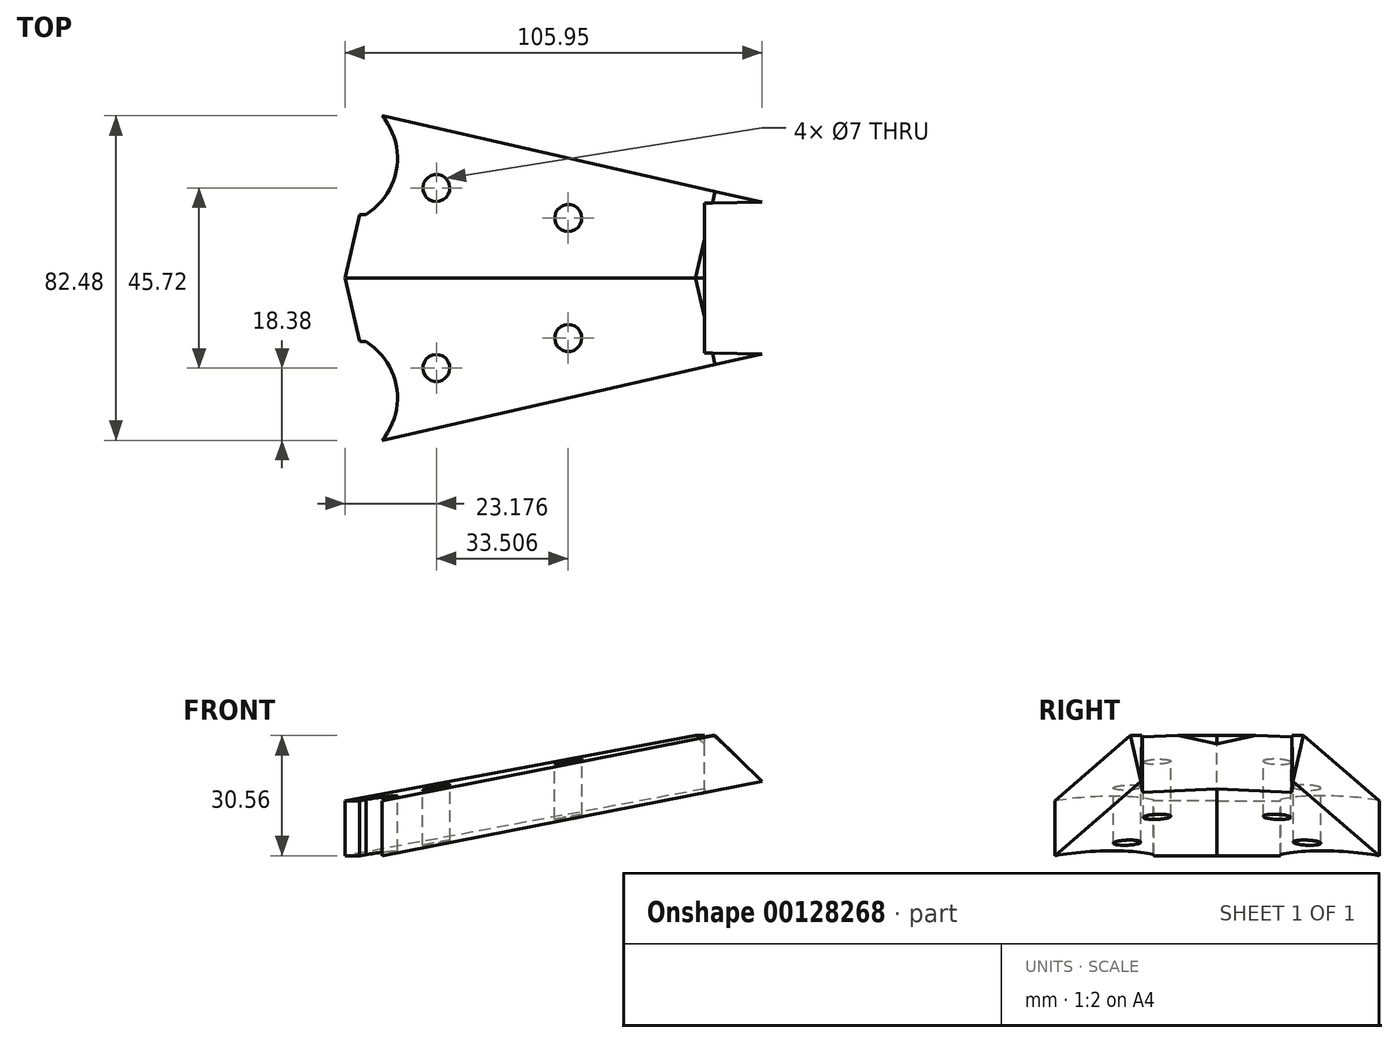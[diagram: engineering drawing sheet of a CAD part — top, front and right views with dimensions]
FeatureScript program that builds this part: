
annotation { "Feature Type Name" : "Feature", "Feature Type Description" : "" }
export const myFeature = defineFeature(function(context is Context, id is Id, definition is map)
    precondition{}
    {
        {
            var Q0;
            Q0=qCreatedBy(makeId("Top.planeOp"),FACE);
            var sketch = newSketch(context, id + "F0", { "sketchPlane" : qUnion([Q0])});
            skLineSegment(sketch, "E0", {"start": v(-293, 0) * mm, "end": v(-293, -19) * mm});
            skPoint(sketch, "E1.end.orphan", {"position": v(0, -123.72) * mm});
            skLineSegment(sketch, "E2", {"start": v(-293, -19) * mm, "end": v(-278.32, -19.28) * mm});
            skLineSegment(sketch, "E3", {"start": v(-394.6, -45.72) * mm, "end": v(-394.6, 0) * mm});
            skLineSegment(sketch, "E4", {"start": v(-293, 0) * mm, "end": v(-394.6, 0) * mm});
            skLineSegment(sketch, "E5", {"start": v(-394.6, -45.72) * mm, "end": v(-278.32, -19.28) * mm});
            skPoint(sketch, "E6.end.orphan", {"position": v(0, 0) * mm});
            skPoint(sketch, "E6.start.orphan", {"position": v(0, -24.5) * mm});
            skCircle(sketch, "E7", {"center": v(-361.1, -22.86) * mm, "radius": 3.5 * mm});
            skCircle(sketch, "E8", {"center": v(-327.59, -15.24) * mm, "radius": 3.5 * mm});
            skArc(sketch, "E9", {"start": v(-394.6, 0) * mm, "mid": v(-390.09, -11.3) * mm, "end": v(-378.93, -16.18) * mm});
            skPoint(sketch, "E9.second.point", {"position": v(-362.57, 0) * mm});
            skPoint(sketch, "E9.third.point", {"position": v(-378.93, -16.18) * mm});
            skArc(sketch, "E10", {"start": v(-374.89, -41.24) * mm, "mid": v(-371.17, -27.78) * mm, "end": v(-378.93, -16.18) * mm});
            skPoint(sketch, "E10.second.point", {"position": v(-374.89, -41.24) * mm});
            skSolve(sketch);
        }
        {
            var Q0;
            {var subQ0=sQuery(id+"F0.wireOp",EDGE,"E0");Q0=makeQuery(id+"F0.imprint","IMPRINT",FACE,{"disambiguationData":[TD([[makeQuery(id+"F0.imprint","IMPRINT",EDGE,{"derivedFrom":subQ0}),-1.0]])]});}
            extrude(context, id + "F1", {"entities" : qUnion([Q0]), "oppositeDirection" : true, "depth" : 32.9 * mm});
        }
        {
            var Q0;
            Q0=makeQuery(id+"F1.opExtrude","SWEPT_FACE",FACE,{"disambiguationData":[OSD([sQuery(id+"F0.wireOp",EDGE,"E5")])]});
            var sketch = newSketch(context, id + "F2", { "sketchPlane" : qUnion([Q0])});
            skPoint(sketch, "E11.end.orphan", {"position": v(-325.18, 0) * mm});
            skLineSegment(sketch, "E12", {"start": v(-287.9, -2.33) * mm, "end": v(-275.66, -14) * mm});
            skLineSegment(sketch, "E13", {"start": v(-275.66, -32.9) * mm, "end": v(-275.66, -32.9) * mm});
            skLineSegment(sketch, "E14", {"start": v(-374.7, -32.9) * mm, "end": v(-275.66, -14) * mm});
            skLineSegment(sketch, "E15", {"start": v(-374.7, -32.9) * mm, "end": v(-374.7, -18.9) * mm});
            skLineSegment(sketch, "E16", {"start": v(-287.9, -2.33) * mm, "end": v(-374.7, -18.9) * mm});
            skPoint(sketch, "E17.orphan", {"position": v(-275.66, 0) * mm});
            skPoint(sketch, "E18.orphan", {"position": v(-374.7, -16.45) * mm});
            skLineSegment(sketch, "E19", {"start": v(-374.7, -18.9) * mm, "end": v(-395.9, -22.94) * mm});
            skSolve(sketch);
        }
        {
            var Q0;
            {var subQ0=sQuery(id+"F2.wireOp",EDGE,"ibXnYeRO-2Iup-lPAK-uRPw-Q9BW2smqNnb0");Q0=makeQuery(id+"F2.imprint","IMPRINT",FACE,{"disambiguationData":[TD([[makeQuery(id+"F2.imprint","IMPRINT",EDGE,{"derivedFrom":subQ0}),-1.0]])]});}
            var Q1;
            {var subQ2=sQuery(id+"F2.wireOp",EDGE,"E14");Q1=makeQuery(id+"F2.imprint","IMPRINT",FACE,{"disambiguationData":[TD([[makeQuery(id+"F2.imprint","IMPRINT",EDGE,{"derivedFrom":subQ2}),-1.0]])]});}
            var Q2;
            {var subQ4=sQuery(id+"F2.wireOp",EDGE,"E12");Q2=makeQuery(id+"F2.imprint","IMPRINT",FACE,{"disambiguationData":[TD([[makeQuery(id+"F2.imprint","IMPRINT",EDGE,{"derivedFrom":subQ4}),1.0]])]});}
            extrude(context, id + "F3", {"entities" : qUnion([Q0, Q1, Q2]), "operationType" : NewBodyOperationType.REMOVE, "endBound" : BoundingType.THROUGH_ALL, "oppositeDirection" : true, "depth" : 25.4 * mm});
        }
        {
            var Q0;
            Q0=makeQuery(id+"F1.opExtrude","SWEPT_BODY",BODY,{"disambiguationData":[OSD([sQuery(id+"F0.wireOp",EDGE,"E2"),sQuery(id+"F0.wireOp",EDGE,"E0"),sQuery(id+"F0.wireOp",EDGE,"E3"),sQuery(id+"F0.wireOp",EDGE,"E4"),sQuery(id+"F0.wireOp",EDGE,"E5")])]});
            var Q1;
            Q1=qCreatedBy(makeId("Front.planeOp"),FACE);
            mirror(context, id + "F4", {"operationType" : NewBodyOperationType.ADD, "entities" : qUnion([Q0]), "mirrorPlane" : qUnion([Q1])});
        }
        {
            var Q0;
            {var subQ0=sQuery(id+"F0.wireOp",EDGE,"E3");var subQ1=sQuery(id+"F0.wireOp",EDGE,"E4");var subQ2=sQuery(id+"F0.wireOp",EDGE,"E9");var subQ3=sQuery(id+"F0.wireOp",EDGE,"E10");var subQ4=sQuery(id+"F0.wireOp",EDGE,"E5");var subQ5=makeQuery(id+"F3.boolean.opBoolean","SPLIT",FACE,{"disambiguationData":[TD([makeQuery(id+"F1.opExtrude","SWEPT_FACE",FACE,{"disambiguationData":[OSD([subQ0])]})])],"derivedFrom":makeQuery(id+"F1.opExtrude","CAP_FACE",FACE,{"disambiguationData":[OSD([sQuery(id+"F0.wireOp",EDGE,"E2"),sQuery(id+"F0.wireOp",EDGE,"E0"),subQ0,subQ1,subQ4,sQuery(id+"F0.wireOp",EDGE,"E7"),sQuery(id+"F0.wireOp",EDGE,"E8"),subQ2,subQ3])],"isStart":true})});Q0=makeQuery(id+"F4.boolean.opBoolean","MERGE",FACE,{"derivedFrom":[subQ5,makeQuery(id+"F4.opPattern","COPY",FACE,{"derivedFrom":subQ5,"instanceName":"1"})]});}
            extrude(context, id + "F5", {"entities" : qUnion([Q0]), "operationType" : NewBodyOperationType.REMOVE, "endBound" : BoundingType.THROUGH_ALL, "oppositeDirection" : true, "depth" : 25.4 * mm});
        }
    });
